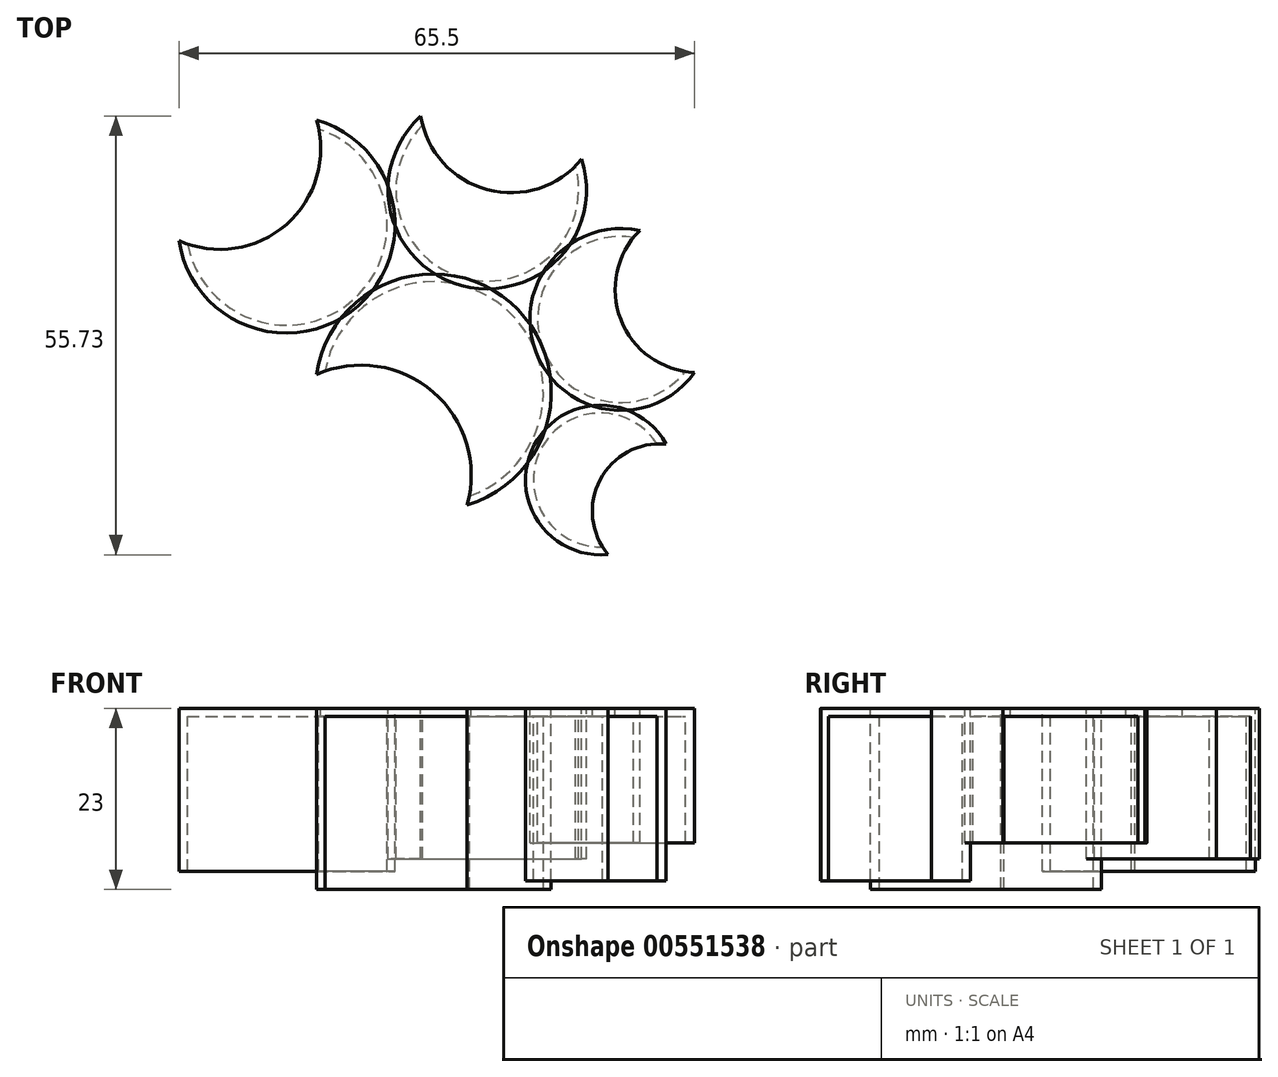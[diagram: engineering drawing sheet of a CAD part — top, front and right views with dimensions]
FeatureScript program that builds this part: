
annotation { "Feature Type Name" : "Feature", "Feature Type Description" : "" }
export const myFeature = defineFeature(function(context is Context, id is Id, definition is map)
    precondition{}
    {
        {
            var Q0;
            Q0=qCreatedBy(makeId("Top.planeOp"),FACE);
            var sketch = newSketch(context, id + "F0", { "sketchPlane" : qUnion([Q0])});
            skCircle(sketch, "E0", {"center": v(-43.53, 14.5) * mm, "radius": 14 * mm});
            skCircle(sketch, "E1", {"center": v(-62.18, 35.78) * mm, "radius": 12.8 * mm});
            skCircle(sketch, "E2", {"center": v(-36.65, 40.19) * mm, "radius": 11.6 * mm});
            skCircle(sketch, "E3", {"center": v(-19.7, 23.7) * mm, "radius": 10.55 * mm});
            skCircle(sketch, "E4", {"center": v(-22.29, 3.3) * mm, "radius": 8.5 * mm});
            skLineSegment(sketch, "E5", {"start": v(-43.53, 14.5) * mm, "end": v(-22.29, 3.3) * mm, "construction": true});
            skLineSegment(sketch, "E6", {"start": v(-22.29, 3.3) * mm, "end": v(-0.78, -8.01) * mm, "construction": true});
            skLineSegment(sketch, "E7", {"start": v(-43.53, 14.5) * mm, "end": v(-19.7, 23.7) * mm, "construction": true});
            skLineSegment(sketch, "E8", {"start": v(-43.53, 14.5) * mm, "end": v(-36.65, 40.19) * mm, "construction": true});
            skLineSegment(sketch, "E9", {"start": v(-43.53, 14.5) * mm, "end": v(-62.18, 35.78) * mm, "construction": true});
            skLineSegment(sketch, "E10", {"start": v(-19.7, 23.7) * mm, "end": v(-0.52, 31.1) * mm, "construction": true});
            skLineSegment(sketch, "E11", {"start": v(-36.65, 40.19) * mm, "end": v(-29.1, 68.39) * mm, "construction": true});
            skLineSegment(sketch, "E12", {"start": v(-62.18, 35.78) * mm, "end": v(-80.16, 56.3) * mm, "construction": true});
            skCircle(sketch, "E13", {"center": v(-14.76, -0.65) * mm, "radius": 8.55 * mm});
            skCircle(sketch, "E14", {"center": v(-9.86, 27.5) * mm, "radius": 10.55 * mm});
            skCircle(sketch, "E15", {"center": v(-33.65, 51.4) * mm, "radius": 11.6 * mm});
            skCircle(sketch, "E16", {"center": v(-70.6, 45.4) * mm, "radius": 12.8 * mm});
            skLineSegment(sketch, "E17", {"start": v(-43.53, 14.5) * mm, "end": v(-75.97, -23.05) * mm, "construction": true});
            skCircle(sketch, "E18", {"center": v(-52.68, 3.9) * mm, "radius": 14 * mm});
            skSolve(sketch);
        }
        {
            var Q0;
            Q0=makeQuery(id+"F0.imprint","IMPRINT",FACE,{"disambiguationData":[TD([[makeQuery(id+"F0.imprint","IMPRINT",EDGE,{"derivedFrom":sQuery(id+"F0.wireOp",EDGE,"E4")}),1.0]])]});
            extrude(context, id + "F1", {"entities" : qUnion([Q0]), "oppositeDirection" : true, "depth" : 20.9 * mm, "offsetDistance" : 25 * mm});
        }
        {
            var Q0;
            Q0=makeQuery(id+"F0.imprint","IMPRINT",FACE,{"disambiguationData":[TD([[makeQuery(id+"F0.imprint","IMPRINT",EDGE,{"derivedFrom":sQuery(id+"F0.wireOp",EDGE,"E3")}),1.0]])]});
            extrude(context, id + "F2", {"entities" : qUnion([Q0]), "oppositeDirection" : true, "depth" : 16.1 * mm, "offsetDistance" : 25 * mm});
        }
        {
            var Q0;
            Q0=makeQuery(id+"F0.imprint","IMPRINT",FACE,{"disambiguationData":[TD([[makeQuery(id+"F0.imprint","IMPRINT",EDGE,{"derivedFrom":sQuery(id+"F0.wireOp",EDGE,"E2")}),1.0]])]});
            extrude(context, id + "F3", {"entities" : qUnion([Q0]), "oppositeDirection" : true, "depth" : 18.1 * mm, "offsetDistance" : 25 * mm});
        }
        {
            var Q0;
            Q0=makeQuery(id+"F0.imprint","IMPRINT",FACE,{"disambiguationData":[TD([[makeQuery(id+"F0.imprint","IMPRINT",EDGE,{"derivedFrom":sQuery(id+"F0.wireOp",EDGE,"E1")}),1.0]])]});
            extrude(context, id + "F4", {"entities" : qUnion([Q0]), "oppositeDirection" : true, "depth" : 19.7 * mm, "offsetDistance" : 25 * mm});
        }
        {
            var Q0;
            {var subQ0=sQuery(id+"F0.wireOp",EDGE,"E0");var subQ1=sQuery(id+"F0.wireOp",EDGE,"m1BmpHz3-Tor0-DD0e-nqZH-24Uh3vNCgnqH");var subQ2=makeQuery(id+"F0.imprint","INTERSECT",VERTEX,{"disambiguationData":[OD(0.0)],"derivedFrom":[subQ1,subQ0]});Q0=makeQuery(id+"F0.imprint","IMPRINT",FACE,{"disambiguationData":[TD([[makeQuery(id+"F0.imprint","IMPRINT",EDGE,{"disambiguationData":[TD([[subQ2,1.0]])],"derivedFrom":subQ1}),-1.0]])]});}
            var Q1;
            Q1=makeQuery(id+"F0.imprint","IMPRINT",FACE,{"disambiguationData":[TD([[makeQuery(id+"F0.imprint","IMPRINT",EDGE,{"derivedFrom":sQuery(id+"F0.wireOp",EDGE,"E0")}),1.0]])]});
            extrude(context, id + "F5", {"entities" : qUnion([Q0, Q1]), "oppositeDirection" : true, "depth" : 22 * mm, "offsetDistance" : 25 * mm});
        }
        {
            var Q0;
            Q0=makeQuery(id+"F1.opExtrude","CAP_FACE",FACE,{"disambiguationData":[OSD([sQuery(id+"F0.wireOp",EDGE,"E4")])],"isStart":false});
            var Q1;
            Q1=makeQuery(id+"F2.opExtrude","CAP_FACE",FACE,{"disambiguationData":[OSD([sQuery(id+"F0.wireOp",EDGE,"E3")])],"isStart":false});
            var Q2;
            Q2=makeQuery(id+"F3.opExtrude","CAP_FACE",FACE,{"disambiguationData":[OSD([sQuery(id+"F0.wireOp",EDGE,"E2")])],"isStart":false});
            var Q3;
            Q3=makeQuery(id+"F4.opExtrude","CAP_FACE",FACE,{"disambiguationData":[OSD([sQuery(id+"F0.wireOp",EDGE,"E1")])],"isStart":false});
            var Q4;
            Q4=makeQuery(id+"F5.opExtrude","CAP_FACE",FACE,{"disambiguationData":[OSD([sQuery(id+"F0.wireOp",EDGE,"E0")])],"isStart":false});
            shell(context, id + "F6", {"entities" : qUnion([Q0, Q1, Q2, Q3, Q4]), "thickness" : 1 * mm, "oppositeDirection" : true});
        }
        {
            var Q0;
            {var subQ0=sQuery(id+"F0.wireOp",EDGE,"E18");var subQ1=sQuery(id+"F0.wireOp",EDGE,"E0");var subQ2=makeQuery(id+"F0.imprint","INTERSECT",VERTEX,{"disambiguationData":[OD(0.0)],"derivedFrom":[subQ1,subQ0]});Q0=makeQuery(id+"F0.imprint","IMPRINT",FACE,{"disambiguationData":[TD([[makeQuery(id+"F0.imprint","IMPRINT",EDGE,{"disambiguationData":[TD([[subQ2,-1.0]])],"derivedFrom":subQ1}),1.0]])]});}
            var Q1;
            {var subQ0=sQuery(id+"F0.wireOp",EDGE,"E18");var subQ1=sQuery(id+"F0.wireOp",EDGE,"E0");var subQ2=makeQuery(id+"F0.imprint","INTERSECT",VERTEX,{"disambiguationData":[OD(0.0)],"derivedFrom":[subQ1,subQ0]});Q1=makeQuery(id+"F0.imprint","IMPRINT",FACE,{"disambiguationData":[TD([[makeQuery(id+"F0.imprint","IMPRINT",EDGE,{"disambiguationData":[TD([[subQ2,-1.0]])],"derivedFrom":subQ1}),-1.0]])]});}
            var Q2;
            {var subQ0=sQuery(id+"F0.wireOp",EDGE,"E15");var subQ1=sQuery(id+"F0.wireOp",EDGE,"E2");var subQ2=makeQuery(id+"F0.imprint","INTERSECT",VERTEX,{"disambiguationData":[OD(0.0)],"derivedFrom":[subQ1,subQ0]});Q2=makeQuery(id+"F0.imprint","IMPRINT",FACE,{"disambiguationData":[TD([[makeQuery(id+"F0.imprint","IMPRINT",EDGE,{"disambiguationData":[TD([[subQ2,1.0]])],"derivedFrom":subQ1}),1.0]])]});}
            var Q3;
            {var subQ0=sQuery(id+"F0.wireOp",EDGE,"E14");var subQ1=sQuery(id+"F0.wireOp",EDGE,"E3");var subQ2=makeQuery(id+"F0.imprint","INTERSECT",VERTEX,{"disambiguationData":[OD(0.0)],"derivedFrom":[subQ1,subQ0]});Q3=makeQuery(id+"F0.imprint","IMPRINT",FACE,{"disambiguationData":[TD([[makeQuery(id+"F0.imprint","IMPRINT",EDGE,{"disambiguationData":[TD([[subQ2,-1.0]])],"derivedFrom":subQ1}),1.0]])]});}
            var Q4;
            {var subQ0=sQuery(id+"F0.wireOp",EDGE,"E13");var subQ1=sQuery(id+"F0.wireOp",EDGE,"E4");var subQ2=makeQuery(id+"F0.imprint","INTERSECT",VERTEX,{"disambiguationData":[OD(0.0)],"derivedFrom":[subQ1,subQ0]});Q4=makeQuery(id+"F0.imprint","IMPRINT",FACE,{"disambiguationData":[TD([[makeQuery(id+"F0.imprint","IMPRINT",EDGE,{"disambiguationData":[TD([[subQ2,-1.0]])],"derivedFrom":subQ1}),1.0]])]});}
            var Q5;
            {var subQ0=sQuery(id+"F0.wireOp",EDGE,"E16");var subQ1=sQuery(id+"F0.wireOp",EDGE,"E1");var subQ2=makeQuery(id+"F0.imprint","INTERSECT",VERTEX,{"disambiguationData":[OD(0.0)],"derivedFrom":[subQ1,subQ0]});Q5=makeQuery(id+"F0.imprint","IMPRINT",FACE,{"disambiguationData":[TD([[makeQuery(id+"F0.imprint","IMPRINT",EDGE,{"disambiguationData":[TD([[subQ2,1.0]])],"derivedFrom":subQ1}),-1.0]])]});}
            extrude(context, id + "F7", {"entities" : qUnion([Q0, Q1, Q2, Q3, Q4, Q5]), "operationType" : NewBodyOperationType.REMOVE, "oppositeDirection" : true, "depth" : 25 * mm, "offsetDistance" : 25 * mm});
        }
        {
            var Q0;
            {var subQ0=sQuery(id+"F0.wireOp",EDGE,"E18");var subQ1=sQuery(id+"F0.wireOp",EDGE,"E0");var subQ2=makeQuery(id+"F0.imprint","INTERSECT",VERTEX,{"disambiguationData":[OD(0.0)],"derivedFrom":[subQ1,subQ0]});Q0=makeQuery(id+"F0.imprint","IMPRINT",FACE,{"disambiguationData":[TD([[makeQuery(id+"F0.imprint","IMPRINT",EDGE,{"disambiguationData":[TD([[subQ2,-1.0]])],"derivedFrom":subQ1}),1.0]])]});}
            var Q1;
            {var subQ0=sQuery(id+"F0.wireOp",EDGE,"E18");var subQ1=sQuery(id+"F0.wireOp",EDGE,"E0");var subQ2=makeQuery(id+"F0.imprint","INTERSECT",VERTEX,{"disambiguationData":[OD(0.0)],"derivedFrom":[subQ1,subQ0]});Q1=makeQuery(id+"F0.imprint","IMPRINT",FACE,{"disambiguationData":[TD([[makeQuery(id+"F0.imprint","IMPRINT",EDGE,{"disambiguationData":[TD([[subQ2,-1.0]])],"derivedFrom":subQ1}),-1.0]])]});}
            var Q2;
            {var subQ0=sQuery(id+"F0.wireOp",EDGE,"E16");var subQ1=sQuery(id+"F0.wireOp",EDGE,"E1");var subQ2=makeQuery(id+"F0.imprint","INTERSECT",VERTEX,{"disambiguationData":[OD(0.0)],"derivedFrom":[subQ1,subQ0]});Q2=makeQuery(id+"F0.imprint","IMPRINT",FACE,{"disambiguationData":[TD([[makeQuery(id+"F0.imprint","IMPRINT",EDGE,{"disambiguationData":[TD([[subQ2,1.0]])],"derivedFrom":subQ1}),1.0]])]});}
            extrude(context, id + "F8", {"entities" : qUnion([Q0, Q1, Q2]), "operationType" : NewBodyOperationType.REMOVE, "depth" : 25 * mm, "offsetDistance" : 25 * mm});
        }
        {
            var Q0;
            {var subQ0=sQuery(id+"F0.wireOp",EDGE,"E16");var subQ1=sQuery(id+"F0.wireOp",EDGE,"E1");var subQ2=makeQuery(id+"F0.imprint","INTERSECT",VERTEX,{"disambiguationData":[OD(0.0)],"derivedFrom":[subQ1,subQ0]});Q0=makeQuery(id+"F0.imprint","IMPRINT",FACE,{"disambiguationData":[TD([[makeQuery(id+"F0.imprint","IMPRINT",EDGE,{"disambiguationData":[TD([[subQ2,1.0]])],"derivedFrom":subQ1}),-1.0]])]});}
            extrude(context, id + "F9", {"entities" : qUnion([Q0]), "operationType" : NewBodyOperationType.REMOVE, "oppositeDirection" : true, "depth" : 25 * mm, "offsetDistance" : 25 * mm});
        }
        {
            var Q0;
            {var subQ0=sQuery(id+"F0.wireOp",EDGE,"E16");var subQ1=sQuery(id+"F0.wireOp",EDGE,"E1");var subQ2=makeQuery(id+"F0.imprint","INTERSECT",VERTEX,{"disambiguationData":[OD(0.0)],"derivedFrom":[subQ1,subQ0]});Q0=makeQuery(id+"F0.imprint","IMPRINT",FACE,{"disambiguationData":[TD([[makeQuery(id+"F0.imprint","IMPRINT",EDGE,{"disambiguationData":[TD([[subQ2,1.0]])],"derivedFrom":subQ1}),-1.0]])]});}
            var Q1;
            {var subQ0=sQuery(id+"F0.wireOp",EDGE,"E16");var subQ1=sQuery(id+"F0.wireOp",EDGE,"E1");var subQ2=makeQuery(id+"F0.imprint","INTERSECT",VERTEX,{"disambiguationData":[OD(0.0)],"derivedFrom":[subQ1,subQ0]});Q1=makeQuery(id+"F0.imprint","IMPRINT",FACE,{"disambiguationData":[TD([[makeQuery(id+"F0.imprint","IMPRINT",EDGE,{"disambiguationData":[TD([[subQ2,1.0]])],"derivedFrom":subQ1}),1.0]])]});}
            extrude(context, id + "F10", {"entities" : qUnion([Q0, Q1]), "operationType" : NewBodyOperationType.REMOVE, "depth" : 25 * mm, "offsetDistance" : 25 * mm});
        }
        {
            var Q0;
            {var subQ0=sQuery(id+"F0.wireOp",EDGE,"E15");var subQ1=sQuery(id+"F0.wireOp",EDGE,"E2");var subQ2=makeQuery(id+"F0.imprint","INTERSECT",VERTEX,{"disambiguationData":[OD(0.0)],"derivedFrom":[subQ1,subQ0]});Q0=makeQuery(id+"F0.imprint","IMPRINT",FACE,{"disambiguationData":[TD([[makeQuery(id+"F0.imprint","IMPRINT",EDGE,{"disambiguationData":[TD([[subQ2,1.0]])],"derivedFrom":subQ1}),1.0]])]});}
            var Q1;
            {var subQ0=sQuery(id+"F0.wireOp",EDGE,"E15");var subQ1=sQuery(id+"F0.wireOp",EDGE,"E2");var subQ2=makeQuery(id+"F0.imprint","INTERSECT",VERTEX,{"disambiguationData":[OD(0.0)],"derivedFrom":[subQ1,subQ0]});Q1=makeQuery(id+"F0.imprint","IMPRINT",FACE,{"disambiguationData":[TD([[makeQuery(id+"F0.imprint","IMPRINT",EDGE,{"disambiguationData":[TD([[subQ2,1.0]])],"derivedFrom":subQ1}),-1.0]])]});}
            extrude(context, id + "F11", {"entities" : qUnion([Q0, Q1]), "operationType" : NewBodyOperationType.REMOVE, "oppositeDirection" : true, "depth" : 25 * mm, "offsetDistance" : 25 * mm});
        }
        {
            var Q0;
            {var subQ0=sQuery(id+"F0.wireOp",EDGE,"E15");var subQ1=sQuery(id+"F0.wireOp",EDGE,"E2");var subQ2=makeQuery(id+"F0.imprint","INTERSECT",VERTEX,{"disambiguationData":[OD(0.0)],"derivedFrom":[subQ1,subQ0]});Q0=makeQuery(id+"F0.imprint","IMPRINT",FACE,{"disambiguationData":[TD([[makeQuery(id+"F0.imprint","IMPRINT",EDGE,{"disambiguationData":[TD([[subQ2,1.0]])],"derivedFrom":subQ1}),1.0]])]});}
            var Q1;
            {var subQ0=sQuery(id+"F0.wireOp",EDGE,"E15");var subQ1=sQuery(id+"F0.wireOp",EDGE,"E2");var subQ2=makeQuery(id+"F0.imprint","INTERSECT",VERTEX,{"disambiguationData":[OD(0.0)],"derivedFrom":[subQ1,subQ0]});Q1=makeQuery(id+"F0.imprint","IMPRINT",FACE,{"disambiguationData":[TD([[makeQuery(id+"F0.imprint","IMPRINT",EDGE,{"disambiguationData":[TD([[subQ2,1.0]])],"derivedFrom":subQ1}),-1.0]])]});}
            extrude(context, id + "F12", {"entities" : qUnion([Q0, Q1]), "operationType" : NewBodyOperationType.REMOVE, "depth" : 25 * mm, "offsetDistance" : 25 * mm});
        }
        {
            var Q0;
            {var subQ0=sQuery(id+"F0.wireOp",EDGE,"E14");var subQ1=sQuery(id+"F0.wireOp",EDGE,"E3");var subQ2=makeQuery(id+"F0.imprint","INTERSECT",VERTEX,{"disambiguationData":[OD(0.0)],"derivedFrom":[subQ1,subQ0]});Q0=makeQuery(id+"F0.imprint","IMPRINT",FACE,{"disambiguationData":[TD([[makeQuery(id+"F0.imprint","IMPRINT",EDGE,{"disambiguationData":[TD([[subQ2,-1.0]])],"derivedFrom":subQ1}),-1.0]])]});}
            var Q1;
            {var subQ0=sQuery(id+"F0.wireOp",EDGE,"E14");var subQ1=sQuery(id+"F0.wireOp",EDGE,"E3");var subQ2=makeQuery(id+"F0.imprint","INTERSECT",VERTEX,{"disambiguationData":[OD(0.0)],"derivedFrom":[subQ1,subQ0]});Q1=makeQuery(id+"F0.imprint","IMPRINT",FACE,{"disambiguationData":[TD([[makeQuery(id+"F0.imprint","IMPRINT",EDGE,{"disambiguationData":[TD([[subQ2,-1.0]])],"derivedFrom":subQ1}),1.0]])]});}
            extrude(context, id + "F13", {"entities" : qUnion([Q0, Q1]), "operationType" : NewBodyOperationType.REMOVE, "oppositeDirection" : true, "depth" : 25 * mm, "offsetDistance" : 25 * mm});
        }
        {
            var Q0;
            {var subQ0=sQuery(id+"F0.wireOp",EDGE,"E14");var subQ1=sQuery(id+"F0.wireOp",EDGE,"E3");var subQ2=makeQuery(id+"F0.imprint","INTERSECT",VERTEX,{"disambiguationData":[OD(0.0)],"derivedFrom":[subQ1,subQ0]});Q0=makeQuery(id+"F0.imprint","IMPRINT",FACE,{"disambiguationData":[TD([[makeQuery(id+"F0.imprint","IMPRINT",EDGE,{"disambiguationData":[TD([[subQ2,-1.0]])],"derivedFrom":subQ1}),-1.0]])]});}
            var Q1;
            {var subQ0=sQuery(id+"F0.wireOp",EDGE,"E14");var subQ1=sQuery(id+"F0.wireOp",EDGE,"E3");var subQ2=makeQuery(id+"F0.imprint","INTERSECT",VERTEX,{"disambiguationData":[OD(0.0)],"derivedFrom":[subQ1,subQ0]});Q1=makeQuery(id+"F0.imprint","IMPRINT",FACE,{"disambiguationData":[TD([[makeQuery(id+"F0.imprint","IMPRINT",EDGE,{"disambiguationData":[TD([[subQ2,-1.0]])],"derivedFrom":subQ1}),1.0]])]});}
            extrude(context, id + "F14", {"entities" : qUnion([Q0, Q1]), "operationType" : NewBodyOperationType.REMOVE, "depth" : 25 * mm, "offsetDistance" : 25 * mm});
        }
        {
            var Q0;
            {var subQ0=sQuery(id+"F0.wireOp",EDGE,"E13");var subQ1=sQuery(id+"F0.wireOp",EDGE,"E4");var subQ2=makeQuery(id+"F0.imprint","INTERSECT",VERTEX,{"disambiguationData":[OD(0.0)],"derivedFrom":[subQ1,subQ0]});Q0=makeQuery(id+"F0.imprint","IMPRINT",FACE,{"disambiguationData":[TD([[makeQuery(id+"F0.imprint","IMPRINT",EDGE,{"disambiguationData":[TD([[subQ2,-1.0]])],"derivedFrom":subQ1}),-1.0]])]});}
            var Q1;
            {var subQ0=sQuery(id+"F0.wireOp",EDGE,"E13");var subQ1=sQuery(id+"F0.wireOp",EDGE,"E4");var subQ2=makeQuery(id+"F0.imprint","INTERSECT",VERTEX,{"disambiguationData":[OD(0.0)],"derivedFrom":[subQ1,subQ0]});Q1=makeQuery(id+"F0.imprint","IMPRINT",FACE,{"disambiguationData":[TD([[makeQuery(id+"F0.imprint","IMPRINT",EDGE,{"disambiguationData":[TD([[subQ2,-1.0]])],"derivedFrom":subQ1}),1.0]])]});}
            extrude(context, id + "F15", {"entities" : qUnion([Q0, Q1]), "operationType" : NewBodyOperationType.REMOVE, "oppositeDirection" : true, "depth" : 25 * mm, "offsetDistance" : 25 * mm});
        }
        {
            var Q0;
            {var subQ0=sQuery(id+"F0.wireOp",EDGE,"E13");var subQ1=sQuery(id+"F0.wireOp",EDGE,"E4");var subQ2=makeQuery(id+"F0.imprint","INTERSECT",VERTEX,{"disambiguationData":[OD(0.0)],"derivedFrom":[subQ1,subQ0]});Q0=makeQuery(id+"F0.imprint","IMPRINT",FACE,{"disambiguationData":[TD([[makeQuery(id+"F0.imprint","IMPRINT",EDGE,{"disambiguationData":[TD([[subQ2,-1.0]])],"derivedFrom":subQ1}),1.0]])]});}
            var Q1;
            {var subQ0=sQuery(id+"F0.wireOp",EDGE,"E13");var subQ1=sQuery(id+"F0.wireOp",EDGE,"E4");var subQ2=makeQuery(id+"F0.imprint","INTERSECT",VERTEX,{"disambiguationData":[OD(0.0)],"derivedFrom":[subQ1,subQ0]});Q1=makeQuery(id+"F0.imprint","IMPRINT",FACE,{"disambiguationData":[TD([[makeQuery(id+"F0.imprint","IMPRINT",EDGE,{"disambiguationData":[TD([[subQ2,-1.0]])],"derivedFrom":subQ1}),-1.0]])]});}
            extrude(context, id + "F16", {"entities" : qUnion([Q0, Q1]), "operationType" : NewBodyOperationType.REMOVE, "depth" : 25 * mm, "offsetDistance" : 25 * mm});
        }
    });
